# Revit family: P200635WX-125c_WRT314TFD_BW
name_source: partatom
category: Specialty Equipment
units: mm (PartAtom-declared; Revit-internal decimal feet)

## family parameters
Always vertical = Yes
Cut with Voids When Loaded = No
Enable Cutting in Views = No
Maintain Annotation Orientation = No
Part Type = Normal
Room Calculation Point = No
Round Connector Dimension = Use Diameter
Shared = No
Work Plane-Based = No

## types (2) — shared parameters
Accent Material = ARCAT - Metal - Steel - Stainless
Amps = 0 A
Back panel material = ARCAT - Metal - Steel - Stainless
Clearance Material = ARCAT - Clearance
Default Elevation = 0"
Depth = 32 1/4"
Description = 28-inch Wide Top Freezer Refrigerator - 14 cu. ft.
Réfrigérateur à congélateur supérieur, 28 po, 14 pi3
Dimension Guide = http://access.whirlpool.com Guide&sku=WRT314TFDB&language=EN
http://access.whirlpool.com Guide&sku=WRT314TFDB&language=EN
Energy Guide = http://access.whirlpool.com Guide&sku=WRT314TFDB&language=EN
http://access.whirlpool.com Guide&sku=WRT314TFDB&language=FR
Family Name = Top Mount
Feature 1 = Optional Icemaker
Machine à glaçons facultative
Feature 2 = Quiet Cooling
Refroidissement silencieux
Feature 3 = Freezer Temperature Controls
Contrôles de température du congélateur
Height = 62 7/8"
Manufacturer = Whirlpool
Voltage = 0 V
Wheel Material = ARCAT - Plastic - Gray
Width = 28"

## per-type parameters (varying)
| type | Body Material | Door Material | Handle Material |
| WRT314TFDW | ARCAT - Metal - Steel - White | ARCAT - Metal - Steel - White | ARCAT - Metal - Steel - White |
| WRT314TFDB | ARCAT - Metal - Steel - Black | ARCAT - Metal - Steel - Black | ARCAT - Metal - Steel - Black - Dark |

note: column(s) folded — value = type name in every type: Model

## geometry (parser evidence)
native form markers: Sweep x4
no freeform markers — native parametric forms only
